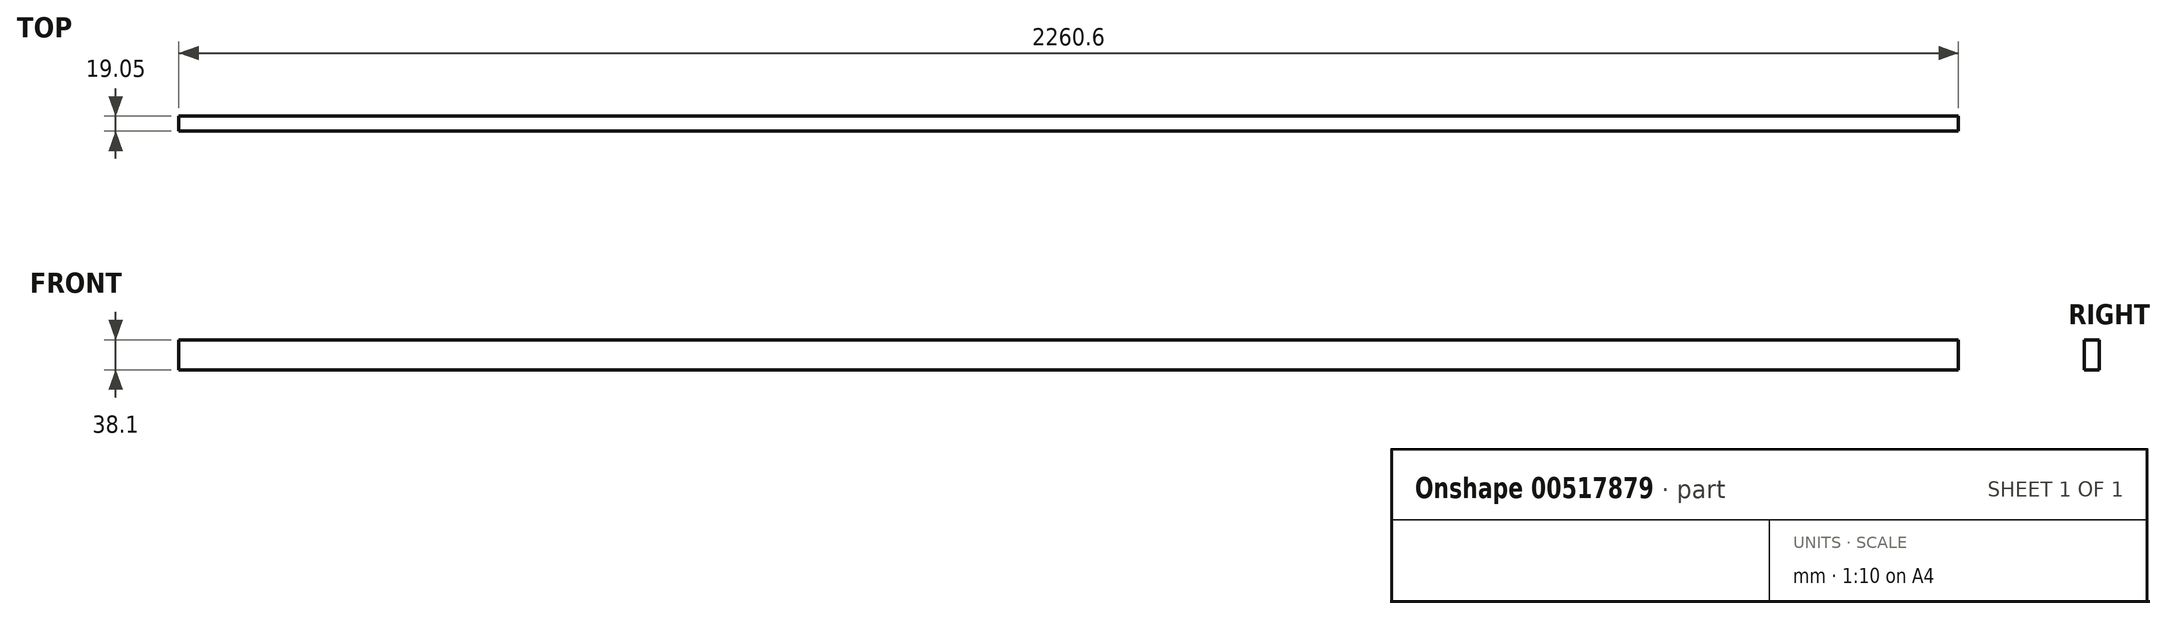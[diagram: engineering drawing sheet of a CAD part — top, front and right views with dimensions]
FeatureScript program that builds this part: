
annotation { "Feature Type Name" : "Feature", "Feature Type Description" : "" }
export const myFeature = defineFeature(function(context is Context, id is Id, definition is map)
    precondition{}
    {
        {
            var Q0;
            Q0=qCreatedBy(makeId("Right.planeOp"),FACE);
            var sketch = newSketch(context, id + "F0", { "sketchPlane" : qUnion([Q0])});
            skLineSegment(sketch, "E0.bottom", {"start": v(0, 0) * mm, "end": v(19.05, 0) * mm});
            skLineSegment(sketch, "E0.top", {"start": v(0, 38.1) * mm, "end": v(19.05, 38.1) * mm});
            skLineSegment(sketch, "E0.left", {"start": v(0, 0) * mm, "end": v(0, 38.1) * mm});
            skLineSegment(sketch, "E0.right", {"start": v(19.05, 0) * mm, "end": v(19.05, 38.1) * mm});
            skSolve(sketch);
        }
        {
            var Q0;
            Q0=makeQuery(id+"F0.imprint","IMPRINT",FACE,{"disambiguationData":[TD([[makeQuery(id+"F0.imprint","IMPRINT",EDGE,{"derivedFrom":sQuery(id+"F0.wireOp",EDGE,"E0.bottom")}),1.0]])]});
            extrude(context, id + "F1", {"entities" : qUnion([Q0]), "oppositeDirection" : true, "depth" : 2260.6 * mm, "offsetDistance" : 25.4 * mm});
        }
    });
